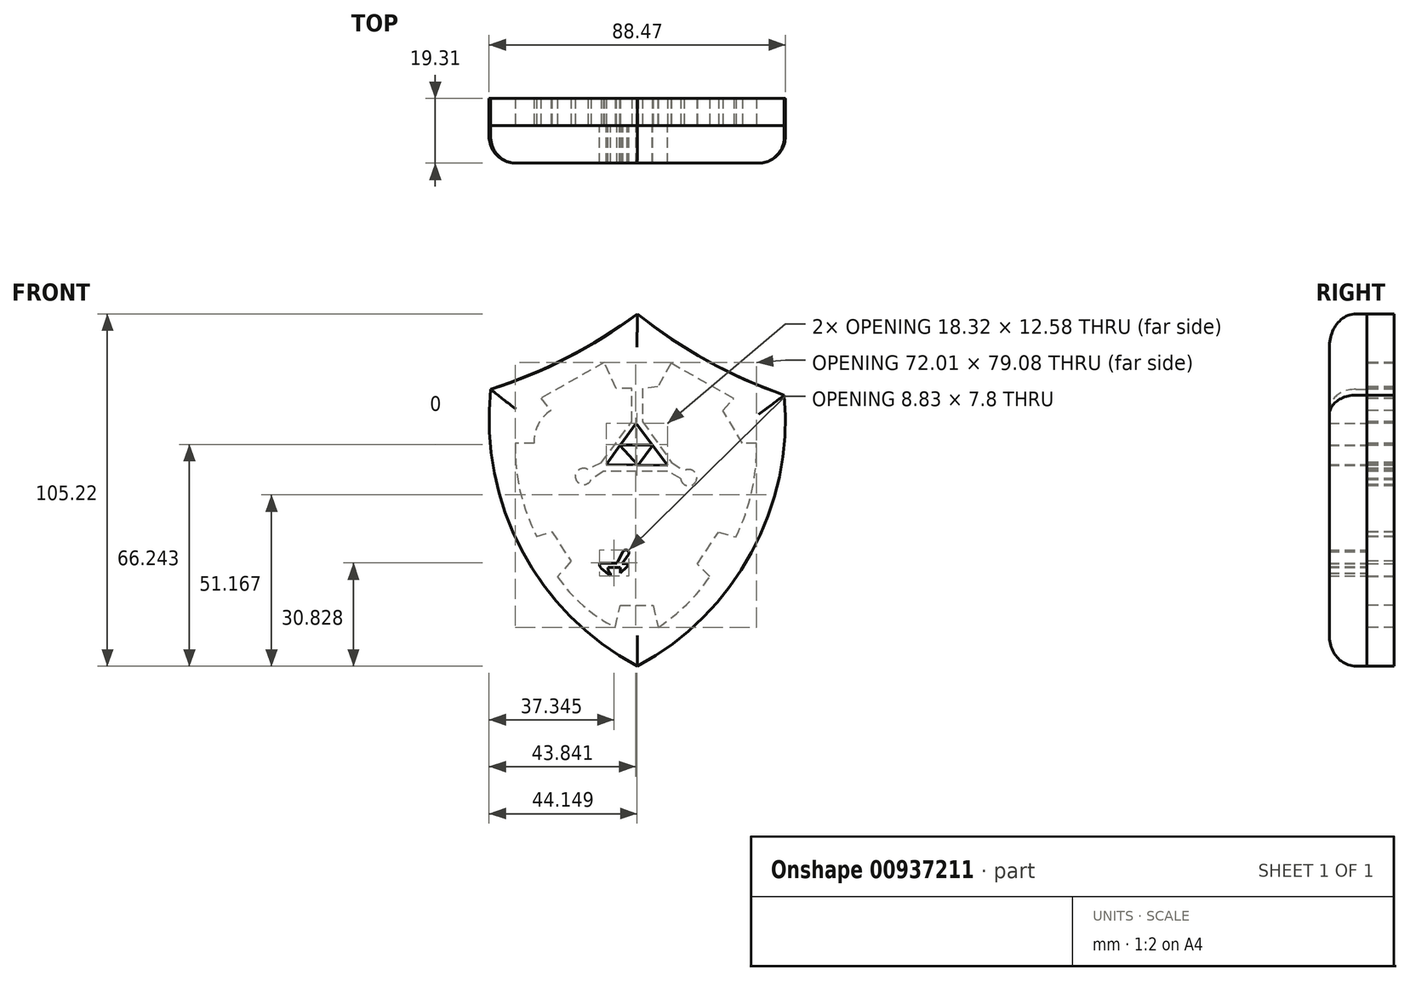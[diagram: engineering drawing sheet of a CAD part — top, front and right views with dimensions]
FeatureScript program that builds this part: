
annotation { "Feature Type Name" : "Feature", "Feature Type Description" : "" }
export const myFeature = defineFeature(function(context is Context, id is Id, definition is map)
    precondition{}
    {
        {
            var Q0;
            Q0=qCreatedBy(makeId("Front.planeOp"),FACE);
            var sketch = newSketch(context, id + "F0", { "sketchPlane" : qUnion([Q0])});
            skArc(sketch, "E0", {"start": v(-56.7, 19.2) * mm, "mid": v(-33.8, 28.57) * mm, "end": v(-12.86, 41.74) * mm});
            skArc(sketch, "E1", {"start": v(-12.86, 41.74) * mm, "mid": v(7.99, 27.67) * mm, "end": v(30.97, 17.46) * mm});
            skArc(sketch, "E2", {"start": v(-12.86, -63.48) * mm, "mid": v(21.2, -29.59) * mm, "end": v(30.97, 17.46) * mm});
            skArc(sketch, "E3", {"start": v(-56.7, 19.2) * mm, "mid": v(-47.44, -28.85) * mm, "end": v(-12.86, -63.48) * mm});
            skLineSegment(sketch, "E4", {"start": v(-8.28, 2.58) * mm, "end": v(-12.7, -3.53) * mm});
            skLineSegment(sketch, "E5", {"start": v(0.36, -13.47) * mm, "end": v(13.66, -8.93) * mm});
            skArc(sketch, "E6", {"start": v(13.66, -8.93) * mm, "mid": v(17.35, -7.44) * mm, "end": v(20.86, -5.56) * mm});
            skArc(sketch, "E7", {"start": v(16.37, -12.5) * mm, "mid": v(19.13, -9.36) * mm, "end": v(20.86, -5.56) * mm});
            skPoint(sketch, "E8", {"position": v(0, -13.58) * mm});
            skLineSegment(sketch, "E9", {"start": v(0, -13.58) * mm, "end": v(0.36, -13.47) * mm});
            skArc(sketch, "E10", {"start": v(0.44, -15.2) * mm, "mid": v(8.46, -14.18) * mm, "end": v(16.37, -12.5) * mm});
            skLineSegment(sketch, "E11", {"start": v(0.44, -15.2) * mm, "end": v(0.44, -17.44) * mm});
            skLineSegment(sketch, "E12", {"start": v(10.97, -17.44) * mm, "end": v(0.44, -17.44) * mm});
            skArc(sketch, "E13", {"start": v(10.97, -17.44) * mm, "mid": v(13.6, -17.2) * mm, "end": v(16.13, -16.53) * mm});
            skLineSegment(sketch, "E14", {"start": v(16.13, -16.53) * mm, "end": v(13.8, -20) * mm});
            skArc(sketch, "E15", {"start": v(0.13, -18.9) * mm, "mid": v(6.9, -20.22) * mm, "end": v(13.8, -20) * mm});
            skArc(sketch, "E16", {"start": v(0.13, -18.9) * mm, "mid": v(-0.5, -19.63) * mm, "end": v(-0.97, -20.5) * mm});
            skLineSegment(sketch, "E17", {"start": v(-0.97, -20.5) * mm, "end": v(6.22, -23.66) * mm});
            skArc(sketch, "E18", {"start": v(6.22, -23.66) * mm, "mid": v(7.7, -24.2) * mm, "end": v(9.22, -24.52) * mm});
            skLineSegment(sketch, "E19", {"start": v(9.22, -24.52) * mm, "end": v(6.35, -25.92) * mm});
            skArc(sketch, "E20", {"start": v(-1.93, -21.78) * mm, "mid": v(1.86, -24.54) * mm, "end": v(6.35, -25.92) * mm});
            skLineSegment(sketch, "E21", {"start": v(-1.93, -21.78) * mm, "end": v(-3.27, -22.73) * mm});
            skLineSegment(sketch, "E22", {"start": v(-3.27, -22.73) * mm, "end": v(-1.17, -26.76) * mm});
            skArc(sketch, "E23", {"start": v(-1.17, -26.76) * mm, "mid": v(-0.43, -27.95) * mm, "end": v(0.5, -29) * mm});
            skLineSegment(sketch, "E24", {"start": v(0.5, -29) * mm, "end": v(-2.2, -29.25) * mm});
            skArc(sketch, "E25", {"start": v(-4.56, -23.5) * mm, "mid": v(-3.82, -26.55) * mm, "end": v(-2.2, -29.25) * mm});
            skArc(sketch, "E26", {"start": v(-8.19, -23.5) * mm, "mid": v(-6.37, -24.18) * mm, "end": v(-4.56, -23.5) * mm});
            skArc(sketch, "E27", {"start": v(-8.44, -20.84) * mm, "mid": v(-8.77, -22.2) * mm, "end": v(-8.19, -23.5) * mm});
            skArc(sketch, "E28", {"start": v(-5.33, -19.98) * mm, "mid": v(-6.92, -20.27) * mm, "end": v(-8.44, -20.84) * mm});
            skArc(sketch, "E29", {"start": v(-5.33, -19.98) * mm, "mid": v(-1.86, -15.18) * mm, "end": v(-3.76, -9.57) * mm});
            skArc(sketch, "E30", {"start": v(0, -13.58) * mm, "mid": v(-1.37, -11.09) * mm, "end": v(-3.76, -9.57) * mm});
            skLineSegment(sketch, "E31", {"start": v(-8.39, -29.34) * mm, "end": v(-6.59, -32.71) * mm});
            skLineSegment(sketch, "E32", {"start": v(-6.59, -32.71) * mm, "end": v(-1.3, -32.71) * mm});
            skLineSegment(sketch, "E33", {"start": v(-8.13, -32.85) * mm, "end": v(-9.98, -30.17) * mm});
            skArc(sketch, "E34", {"start": v(-8.39, -29.34) * mm, "mid": v(-9.65, -28.85) * mm, "end": v(-9.98, -30.17) * mm});
            skLineSegment(sketch, "E35", {"start": v(-8.13, -32.85) * mm, "end": v(-9.24, -32.85) * mm});
            skArc(sketch, "E36", {"start": v(-9.24, -32.85) * mm, "mid": v(-9.74, -33.2) * mm, "end": v(-9.58, -33.79) * mm});
            skLineSegment(sketch, "E37", {"start": v(-9.58, -33.79) * mm, "end": v(-7.63, -35.66) * mm});
            skLineSegment(sketch, "E38", {"start": v(-7.63, -35.66) * mm, "end": v(-7.63, -34.03) * mm});
            skLineSegment(sketch, "E39", {"start": v(-7.63, -34.03) * mm, "end": v(-3.83, -34.03) * mm});
            skArc(sketch, "E40", {"start": v(-4.68, -35.83) * mm, "mid": v(-4.08, -35.02) * mm, "end": v(-3.83, -34.03) * mm});
            skLineSegment(sketch, "E41", {"start": v(-4.68, -35.83) * mm, "end": v(-4.68, -36.55) * mm});
            skLineSegment(sketch, "E42", {"start": v(-4.68, -36.55) * mm, "end": v(-1.91, -34.23) * mm});
            skArc(sketch, "E43", {"start": v(-1.91, -34.23) * mm, "mid": v(-1.42, -33.55) * mm, "end": v(-1.3, -32.71) * mm});
            skLineSegment(sketch, "E44", {"start": v(-12.77, -41.9) * mm, "end": v(-12.13, -38.72) * mm});
            skLineSegment(sketch, "E45", {"start": v(-12.13, -38.72) * mm, "end": v(-11.11, -36.54) * mm});
            skLineSegment(sketch, "E46", {"start": v(-11.11, -36.54) * mm, "end": v(-11.72, -35.83) * mm});
            skLineSegment(sketch, "E47", {"start": v(-11.72, -35.83) * mm, "end": v(-11.72, -32.64) * mm});
            skLineSegment(sketch, "E48", {"start": v(-11.72, -32.64) * mm, "end": v(-11.11, -31.73) * mm});
            skLineSegment(sketch, "E49", {"start": v(-11.11, -31.73) * mm, "end": v(-11.72, -30.74) * mm});
            skArc(sketch, "E50", {"start": v(-10.16, -27.48) * mm, "mid": v(-11.6, -28.8) * mm, "end": v(-11.72, -30.74) * mm});
            skLineSegment(sketch, "E51", {"start": v(-10.16, -27.48) * mm, "end": v(-7.35, -26.45) * mm});
            skLineSegment(sketch, "E52", {"start": v(-7.35, -26.45) * mm, "end": v(-8.57, -26.06) * mm});
            skArc(sketch, "E53", {"start": v(-10.33, -23.17) * mm, "mid": v(-9.98, -24.94) * mm, "end": v(-8.57, -26.06) * mm});
            skLineSegment(sketch, "E54", {"start": v(-10.33, -23.17) * mm, "end": v(-12.43, -21.3) * mm});
            skLineSegment(sketch, "E55", {"start": v(-12.43, -21.3) * mm, "end": v(-12.77, -20.09) * mm});
            skLineSegment(sketch, "E56.MirrorCS", {"start": v(-13.11, -21.3) * mm, "end": v(-12.77, -20.09) * mm});
            skLineSegment(sketch, "E57.MirrorCS", {"start": v(-15.22, -23.17) * mm, "end": v(-13.11, -21.3) * mm});
            skArc(sketch, "E58.MirrorCS", {"start": v(-15.22, -23.17) * mm, "mid": v(-15.57, -24.94) * mm, "end": v(-16.98, -26.06) * mm});
            skLineSegment(sketch, "E59.MirrorCS", {"start": v(-18.2, -26.45) * mm, "end": v(-16.98, -26.06) * mm});
            skLineSegment(sketch, "E60.MirrorCS", {"start": v(-15.39, -27.48) * mm, "end": v(-18.2, -26.45) * mm});
            skArc(sketch, "E61.MirrorCS", {"start": v(-15.39, -27.48) * mm, "mid": v(-13.94, -28.8) * mm, "end": v(-13.83, -30.74) * mm});
            skLineSegment(sketch, "E62.MirrorCS", {"start": v(-14.44, -31.73) * mm, "end": v(-13.83, -30.74) * mm});
            skLineSegment(sketch, "E63.MirrorCS", {"start": v(-13.83, -32.64) * mm, "end": v(-14.44, -31.73) * mm});
            skLineSegment(sketch, "E64.MirrorCS", {"start": v(-13.83, -35.83) * mm, "end": v(-13.83, -32.64) * mm});
            skLineSegment(sketch, "E65.MirrorCS", {"start": v(-14.44, -36.54) * mm, "end": v(-13.83, -35.83) * mm});
            skLineSegment(sketch, "E66.MirrorCS", {"start": v(-13.42, -38.72) * mm, "end": v(-14.44, -36.54) * mm});
            skLineSegment(sketch, "E67.MirrorCS", {"start": v(-12.77, -41.9) * mm, "end": v(-13.42, -38.72) * mm});
            skLineSegment(sketch, "E68", {"start": v(-13.2, -19.23) * mm, "end": v(-12.64, -19.23) * mm});
            skLineSegment(sketch, "E69", {"start": v(-12.64, -19.23) * mm, "end": v(-12.64, -17.45) * mm});
            skArc(sketch, "E70", {"start": v(-11.68, -17.77) * mm, "mid": v(-12.07, -17.33) * mm, "end": v(-12.64, -17.45) * mm});
            skLineSegment(sketch, "E71", {"start": v(-11.68, -17.77) * mm, "end": v(-11.2, -16.54) * mm});
            skLineSegment(sketch, "E72", {"start": v(-11.2, -16.54) * mm, "end": v(-10.34, -17.77) * mm});
            skArc(sketch, "E73", {"start": v(-10.34, -17.77) * mm, "mid": v(-9.81, -17.81) * mm, "end": v(-9.86, -17.29) * mm});
            skArc(sketch, "E74", {"start": v(-10.17, -15.87) * mm, "mid": v(-10.2, -16.62) * mm, "end": v(-9.86, -17.29) * mm});
            skArc(sketch, "E75", {"start": v(-8.7, -17.29) * mm, "mid": v(-9.17, -16.3) * mm, "end": v(-10.17, -15.87) * mm});
            skArc(sketch, "E76", {"start": v(-8.7, -17.29) * mm, "mid": v(-8.49, -17.56) * mm, "end": v(-8.27, -17.29) * mm});
            skArc(sketch, "E77", {"start": v(-8.27, -17.29) * mm, "mid": v(-8.93, -15.3) * mm, "end": v(-10, -13.52) * mm});
            skArc(sketch, "E78", {"start": v(-12.64, -9.75) * mm, "mid": v(-11.92, -12.06) * mm, "end": v(-10, -13.52) * mm});
            skArc(sketch, "E79", {"start": v(-12.64, -9.75) * mm, "mid": v(-12.94, -9.54) * mm, "end": v(-13.24, -9.75) * mm});
            skArc(sketch, "E80.MirrorCS", {"start": v(-13.24, -9.75) * mm, "mid": v(-13.96, -12.06) * mm, "end": v(-15.88, -13.52) * mm});
            skArc(sketch, "E81.MirrorCS", {"start": v(-17.6, -17.29) * mm, "mid": v(-16.96, -15.3) * mm, "end": v(-15.88, -13.52) * mm});
            skArc(sketch, "E82.MirrorCS", {"start": v(-17.18, -17.29) * mm, "mid": v(-17.4, -17.56) * mm, "end": v(-17.6, -17.29) * mm});
            skArc(sketch, "E83.MirrorCS", {"start": v(-17.18, -17.29) * mm, "mid": v(-16.7, -16.3) * mm, "end": v(-15.71, -15.87) * mm});
            skArc(sketch, "E84.MirrorCS", {"start": v(-15.71, -15.87) * mm, "mid": v(-15.67, -16.62) * mm, "end": v(-16.02, -17.29) * mm});
            skArc(sketch, "E85.MirrorCS", {"start": v(-15.54, -17.77) * mm, "mid": v(-16.07, -17.81) * mm, "end": v(-16.02, -17.29) * mm});
            skLineSegment(sketch, "E86.MirrorCS", {"start": v(-14.68, -16.54) * mm, "end": v(-15.54, -17.77) * mm});
            skLineSegment(sketch, "E87.MirrorCS", {"start": v(-14.2, -17.77) * mm, "end": v(-14.68, -16.54) * mm});
            skArc(sketch, "E88.MirrorCS", {"start": v(-14.2, -17.77) * mm, "mid": v(-13.81, -17.33) * mm, "end": v(-13.24, -17.45) * mm});
            skLineSegment(sketch, "E89.MirrorCS", {"start": v(-13.24, -19.23) * mm, "end": v(-13.24, -17.45) * mm});
            skArc(sketch, "E90.MirrorCS", {"start": v(-17.16, -29.34) * mm, "mid": v(-15.9, -28.85) * mm, "end": v(-15.56, -30.17) * mm});
            skLineSegment(sketch, "E91.MirrorCS", {"start": v(-17.16, -29.34) * mm, "end": v(-18.96, -32.71) * mm});
            skLineSegment(sketch, "E92.MirrorCS", {"start": v(-17.42, -32.85) * mm, "end": v(-15.56, -30.17) * mm});
            skLineSegment(sketch, "E93.MirrorCS", {"start": v(-17.42, -32.85) * mm, "end": v(-16.3, -32.85) * mm});
            skArc(sketch, "E94.MirrorCS", {"start": v(-16.3, -32.85) * mm, "mid": v(-15.81, -33.2) * mm, "end": v(-15.97, -33.79) * mm});
            skLineSegment(sketch, "E95.MirrorCS", {"start": v(-15.97, -33.79) * mm, "end": v(-17.92, -35.66) * mm});
            skLineSegment(sketch, "E96.MirrorCS", {"start": v(-17.92, -35.66) * mm, "end": v(-17.92, -34.03) * mm});
            skLineSegment(sketch, "E97.MirrorCS", {"start": v(-17.92, -34.03) * mm, "end": v(-21.72, -34.03) * mm});
            skArc(sketch, "E98.MirrorCS", {"start": v(-20.86, -35.83) * mm, "mid": v(-21.47, -35.02) * mm, "end": v(-21.72, -34.03) * mm});
            skLineSegment(sketch, "E99.MirrorCS", {"start": v(-20.86, -35.83) * mm, "end": v(-20.86, -36.55) * mm});
            skLineSegment(sketch, "E100.MirrorCS", {"start": v(-20.86, -36.55) * mm, "end": v(-23.64, -34.23) * mm});
            skArc(sketch, "E101.MirrorCS", {"start": v(-23.64, -34.23) * mm, "mid": v(-24.13, -33.55) * mm, "end": v(-24.24, -32.71) * mm});
            skLineSegment(sketch, "E102.MirrorCS", {"start": v(-18.96, -32.71) * mm, "end": v(-24.24, -32.71) * mm});
            skArc(sketch, "E103.MirrorCS", {"start": v(-25.75, -14) * mm, "mid": v(-24.47, -11.47) * mm, "end": v(-22.12, -9.87) * mm});
            skLineSegment(sketch, "E104.MirrorCS", {"start": v(-26.12, -13.9) * mm, "end": v(-39.55, -9.8) * mm});
            skArc(sketch, "E105.MirrorCS", {"start": v(-39.55, -9.8) * mm, "mid": v(-43.3, -8.43) * mm, "end": v(-46.86, -6.67) * mm});
            skArc(sketch, "E106.MirrorCS", {"start": v(-42.15, -13.45) * mm, "mid": v(-45.01, -10.4) * mm, "end": v(-46.86, -6.67) * mm});
            skArc(sketch, "E107.MirrorCS", {"start": v(-26.14, -15.64) * mm, "mid": v(-34.19, -14.87) * mm, "end": v(-42.15, -13.45) * mm});
            skLineSegment(sketch, "E108.MirrorCS", {"start": v(-26.14, -15.64) * mm, "end": v(-26.07, -17.87) * mm});
            skLineSegment(sketch, "E109.MirrorCS", {"start": v(-36.6, -18.21) * mm, "end": v(-26.07, -17.87) * mm});
            skArc(sketch, "E110.MirrorCS", {"start": v(-36.6, -18.21) * mm, "mid": v(-39.22, -18.07) * mm, "end": v(-41.78, -17.47) * mm});
            skLineSegment(sketch, "E111.MirrorCS", {"start": v(-41.78, -17.47) * mm, "end": v(-39.34, -20.87) * mm});
            skArc(sketch, "E112.MirrorCS", {"start": v(-25.71, -19.32) * mm, "mid": v(-32.44, -20.86) * mm, "end": v(-39.34, -20.87) * mm});
            skArc(sketch, "E113.MirrorCS", {"start": v(-25.71, -19.32) * mm, "mid": v(-25.05, -20.03) * mm, "end": v(-24.56, -20.88) * mm});
            skArc(sketch, "E114.MirrorCS", {"start": v(-23.56, -22.13) * mm, "mid": v(-27.26, -25) * mm, "end": v(-31.7, -26.54) * mm});
            skLineSegment(sketch, "E115.MirrorCS", {"start": v(-24.56, -20.88) * mm, "end": v(-31.65, -24.28) * mm});
            skLineSegment(sketch, "E116.MirrorCS", {"start": v(-34.62, -25.24) * mm, "end": v(-31.7, -26.54) * mm});
            skArc(sketch, "E117.MirrorCS", {"start": v(-31.65, -24.28) * mm, "mid": v(-33.1, -24.86) * mm, "end": v(-34.62, -25.24) * mm});
            skLineSegment(sketch, "E118.MirrorCS", {"start": v(-22.19, -23.03) * mm, "end": v(-24.16, -27.14) * mm});
            skLineSegment(sketch, "E119.MirrorCS", {"start": v(-23.56, -22.13) * mm, "end": v(-22.19, -23.03) * mm});
            skArc(sketch, "E120.MirrorCS", {"start": v(-24.16, -27.14) * mm, "mid": v(-24.86, -28.35) * mm, "end": v(-25.75, -29.43) * mm});
            skLineSegment(sketch, "E121.MirrorCS", {"start": v(-25.75, -29.43) * mm, "end": v(-23.05, -29.6) * mm});
            skArc(sketch, "E122.MirrorCS", {"start": v(-20.87, -23.76) * mm, "mid": v(-21.51, -26.84) * mm, "end": v(-23.05, -29.6) * mm});
            skArc(sketch, "E123.MirrorCS", {"start": v(-17.25, -23.64) * mm, "mid": v(-19.04, -24.39) * mm, "end": v(-20.87, -23.76) * mm});
            skArc(sketch, "E124.MirrorCS", {"start": v(-17.08, -20.98) * mm, "mid": v(-16.7, -22.34) * mm, "end": v(-17.25, -23.64) * mm});
            skArc(sketch, "E125.MirrorCS", {"start": v(-20.22, -20.22) * mm, "mid": v(-18.61, -20.47) * mm, "end": v(-17.08, -20.98) * mm});
            skArc(sketch, "E126.MirrorCS", {"start": v(-20.22, -20.22) * mm, "mid": v(-23.84, -15.54) * mm, "end": v(-22.12, -9.87) * mm});
            skArc(sketch, "E127", {"start": v(12.96, -0.92) * mm, "mid": v(8.7, 10.6) * mm, "end": v(-1.1, 17.98) * mm});
            skArc(sketch, "E128", {"start": v(15.67, -1.42) * mm, "mid": v(10.69, 11.21) * mm, "end": v(-1.1, 17.98) * mm});
            skLineSegment(sketch, "E129", {"start": v(15.67, -1.42) * mm, "end": v(16.88, -3.2) * mm});
            skLineSegment(sketch, "E130", {"start": v(16.88, -3.2) * mm, "end": v(8.75, -5.13) * mm});
            skArc(sketch, "E131", {"start": v(8.75, -5.13) * mm, "mid": v(5.7, -1.88) * mm, "end": v(1.26, -1.7) * mm});
            skLineSegment(sketch, "E132", {"start": v(1.26, -1.7) * mm, "end": v(-6.09, 7.14) * mm});
            skArc(sketch, "E133", {"start": v(-6.09, 7.14) * mm, "mid": v(-5.36, 10.6) * mm, "end": v(-8.3, 12.56) * mm});
            skLineSegment(sketch, "E134", {"start": v(-8.3, 12.56) * mm, "end": v(-9.94, 12.55) * mm});
            skLineSegment(sketch, "E135", {"start": v(-9.94, 12.55) * mm, "end": v(-8.3, 13.91) * mm});
            skArc(sketch, "E136", {"start": v(-3.23, 8.13) * mm, "mid": v(-3.65, 12.88) * mm, "end": v(-8.3, 13.91) * mm});
            skLineSegment(sketch, "E137", {"start": v(-3.23, 8.13) * mm, "end": v(1.69, 2.71) * mm});
            skPoint(sketch, "E137.endSnap0", {"position": v(-2.41, 2.71) * mm});
            skArc(sketch, "E138", {"start": v(9.75, -0.7) * mm, "mid": v(6.62, 3.11) * mm, "end": v(1.69, 2.71) * mm});
            skLineSegment(sketch, "E139", {"start": v(9.75, -0.7) * mm, "end": v(12.96, -0.92) * mm});
            skLineSegment(sketch, "E140.MirrorCS", {"start": v(-16.36, 12.55) * mm, "end": v(-18, 13.91) * mm});
            skLineSegment(sketch, "E141.MirrorCS", {"start": v(-18, 12.56) * mm, "end": v(-16.36, 12.55) * mm});
            skArc(sketch, "E142.MirrorCS", {"start": v(-20.22, 7.14) * mm, "mid": v(-20.94, 10.6) * mm, "end": v(-18, 12.56) * mm});
            skLineSegment(sketch, "E143.MirrorCS", {"start": v(-27.56, -1.7) * mm, "end": v(-20.22, 7.14) * mm});
            skArc(sketch, "E144.MirrorCS", {"start": v(-35.05, -5.13) * mm, "mid": v(-32.01, -1.88) * mm, "end": v(-27.56, -1.7) * mm});
            skLineSegment(sketch, "E145.MirrorCS", {"start": v(-43.18, -3.2) * mm, "end": v(-35.05, -5.13) * mm});
            skLineSegment(sketch, "E146.MirrorCS", {"start": v(-41.97, -1.42) * mm, "end": v(-43.18, -3.2) * mm});
            skArc(sketch, "E147.MirrorCS", {"start": v(-41.97, -1.42) * mm, "mid": v(-36.99, 11.21) * mm, "end": v(-25.2, 17.98) * mm});
            skArc(sketch, "E148.MirrorCS", {"start": v(-39.26, -0.92) * mm, "mid": v(-35, 10.6) * mm, "end": v(-25.2, 17.98) * mm});
            skLineSegment(sketch, "E149.MirrorCS", {"start": v(-36.05, -0.7) * mm, "end": v(-39.26, -0.92) * mm});
            skArc(sketch, "E150.MirrorCS", {"start": v(-36.05, -0.7) * mm, "mid": v(-32.92, 3.11) * mm, "end": v(-27.99, 2.71) * mm});
            skLineSegment(sketch, "E151.MirrorCS", {"start": v(-23.07, 8.13) * mm, "end": v(-27.99, 2.71) * mm});
            skArc(sketch, "E152.MirrorCS", {"start": v(-23.07, 8.13) * mm, "mid": v(-22.65, 12.88) * mm, "end": v(-18, 13.91) * mm});
            skLineSegment(sketch, "E153", {"start": v(-13.24, 9.05) * mm, "end": v(-3.87, -3.53) * mm});
            skLineSegment(sketch, "E154", {"start": v(-13.24, 9.05) * mm, "end": v(-22.2, -3.26) * mm});
            skLineSegment(sketch, "E155", {"start": v(-22.2, -3.26) * mm, "end": v(-3.87, -3.53) * mm});
            skLineSegment(sketch, "E156", {"start": v(-11.37, 19.49) * mm, "end": v(-11.37, 9.56) * mm});
            skLineSegment(sketch, "E157", {"start": v(-11.37, 9.56) * mm, "end": v(-2.72, -2.65) * mm});
            skLineSegment(sketch, "E158", {"start": v(-2.72, -2.65) * mm, "end": v(1.01, -5.2) * mm});
            skArc(sketch, "E159", {"start": v(0, -7.4) * mm, "mid": v(4.64, -8.2) * mm, "end": v(1.01, -5.2) * mm});
            skLineSegment(sketch, "E160", {"start": v(-12.7, -5.26) * mm, "end": v(-3.91, -5.26) * mm});
            skLineSegment(sketch, "E161", {"start": v(0, -7.4) * mm, "end": v(-3.91, -5.26) * mm});
            skLineSegment(sketch, "E162", {"start": v(-23.69, -2.73) * mm, "end": v(-27.68, -4.76) * mm});
            skArc(sketch, "E163", {"start": v(-27.68, -4.76) * mm, "mid": v(-31.3, -7.56) * mm, "end": v(-26.73, -7.81) * mm});
            skLineSegment(sketch, "E164", {"start": v(-23.69, -2.73) * mm, "end": v(-14.52, 9.56) * mm});
            skLineSegment(sketch, "E165", {"start": v(-14.52, 9.56) * mm, "end": v(-14.52, 19.52) * mm});
            skLineSegment(sketch, "E166", {"start": v(-8.55, -41.43) * mm, "end": v(-5.77, -41.43) * mm});
            skLineSegment(sketch, "E167", {"start": v(-5.77, -41.43) * mm, "end": v(-4.41, -45.04) * mm});
            skLineSegment(sketch, "E168", {"start": v(-8.55, -41.43) * mm, "end": v(-8.55, -42.23) * mm});
            skLineSegment(sketch, "E169", {"start": v(-8.55, -42.23) * mm, "end": v(-6.78, -42.23) * mm});
            skLineSegment(sketch, "E170", {"start": v(-6.78, -42.23) * mm, "end": v(-5.1, -47.88) * mm});
            skPoint(sketch, "E170.endSnap0", {"position": v(-5.1, -43.23) * mm});
            skLineSegment(sketch, "E171", {"start": v(-5.1, -47.88) * mm, "end": v(-2.5, -45.77) * mm});
            skArc(sketch, "E172", {"start": v(-2.5, -45.77) * mm, "mid": v(1.76, -41.27) * mm, "end": v(4.72, -35.83) * mm});
            skArc(sketch, "E173", {"start": v(-4.41, -45.04) * mm, "mid": v(0.42, -40.7) * mm, "end": v(4.72, -35.83) * mm});
            skLineSegment(sketch, "E174", {"start": v(-17.4, -42.56) * mm, "end": v(-20.53, -42.56) * mm});
            skLineSegment(sketch, "E175", {"start": v(-20.53, -42.56) * mm, "end": v(-20.53, -47.92) * mm});
            skArc(sketch, "E176", {"start": v(-30.91, -35.37) * mm, "mid": v(-27.02, -42.72) * mm, "end": v(-20.53, -47.92) * mm});
            skArc(sketch, "E177", {"start": v(-30.91, -35.37) * mm, "mid": v(-26.87, -40.23) * mm, "end": v(-22.07, -44.34) * mm});
            skLineSegment(sketch, "E178", {"start": v(-17.4, -42.56) * mm, "end": v(-17.4, -40.8) * mm});
            skLineSegment(sketch, "E179", {"start": v(-17.4, -40.8) * mm, "end": v(-20.8, -40.8) * mm});
            skLineSegment(sketch, "E180", {"start": v(-20.8, -40.8) * mm, "end": v(-22.07, -44.34) * mm});
            skLineSegment(sketch, "E181", {"start": v(-26.12, -13.9) * mm, "end": v(-25.75, -14) * mm});
            skLineSegment(sketch, "E182", {"start": v(-13.24, -19.23) * mm, "end": v(-13.2, -19.23) * mm});
            skLineSegment(sketch, "E183", {"start": v(-12.7, -5.26) * mm, "end": v(-23, -5.26) * mm});
            skLineSegment(sketch, "E184", {"start": v(-23, -5.26) * mm, "end": v(-26.73, -7.81) * mm});
            skLineSegment(sketch, "E185", {"start": v(-14.52, 19.52) * mm, "end": v(-19.3, 19.52) * mm});
            skLineSegment(sketch, "E186", {"start": v(-19.3, 19.52) * mm, "end": v(-22.8, 27.23) * mm});
            skLineSegment(sketch, "E187", {"start": v(-22.8, 27.23) * mm, "end": v(-41.67, 16.51) * mm});
            skLineSegment(sketch, "E188", {"start": v(-41.67, 16.51) * mm, "end": v(-38.73, 12.85) * mm});
            skArc(sketch, "E189", {"start": v(-38.73, 12.85) * mm, "mid": v(-42.53, 8.63) * mm, "end": v(-43.7, 3.08) * mm});
            skLineSegment(sketch, "E190", {"start": v(-43.7, 3.08) * mm, "end": v(-49.35, 3.08) * mm});
            skArc(sketch, "E191", {"start": v(-49.35, 3.08) * mm, "mid": v(-47.88, -11.24) * mm, "end": v(-42.93, -24.75) * mm});
            skLineSegment(sketch, "E192", {"start": v(-42.93, -24.75) * mm, "end": v(-38.46, -23.27) * mm});
            skLineSegment(sketch, "E193", {"start": v(-38.46, -23.27) * mm, "end": v(-32.68, -32.15) * mm});
            skLineSegment(sketch, "E194", {"start": v(-32.68, -32.15) * mm, "end": v(-36.74, -36.78) * mm});
            skArc(sketch, "E195", {"start": v(-36.74, -36.78) * mm, "mid": v(-29.08, -45.38) * mm, "end": v(-19.56, -51.85) * mm});
            skLineSegment(sketch, "E196", {"start": v(-19.56, -51.85) * mm, "end": v(-17.92, -45.29) * mm});
            skLineSegment(sketch, "E197", {"start": v(-17.92, -45.29) * mm, "end": v(-8.22, -45.29) * mm});
            skLineSegment(sketch, "E198", {"start": v(-8.22, -45.29) * mm, "end": v(-6.65, -51.85) * mm});
            skArc(sketch, "E199", {"start": v(-6.65, -51.85) * mm, "mid": v(1.8, -45.06) * mm, "end": v(8.76, -36.73) * mm});
            skLineSegment(sketch, "E200", {"start": v(8.76, -36.73) * mm, "end": v(4.98, -32.95) * mm});
            skLineSegment(sketch, "E201", {"start": v(4.98, -32.95) * mm, "end": v(11.33, -23.46) * mm});
            skLineSegment(sketch, "E202", {"start": v(11.33, -23.46) * mm, "end": v(16.53, -24.9) * mm});
            skArc(sketch, "E203", {"start": v(16.53, -24.9) * mm, "mid": v(21.27, -11.28) * mm, "end": v(22.67, 3.07) * mm});
            skLineSegment(sketch, "E204", {"start": v(22.67, 3.07) * mm, "end": v(18.53, 3.07) * mm});
            skLineSegment(sketch, "E205", {"start": v(18.53, 3.07) * mm, "end": v(12.68, 12.84) * mm});
            skLineSegment(sketch, "E206", {"start": v(12.68, 12.84) * mm, "end": v(15.9, 16.48) * mm});
            skLineSegment(sketch, "E207", {"start": v(15.9, 16.48) * mm, "end": v(-2.87, 26.96) * mm});
            skLineSegment(sketch, "E208", {"start": v(-2.87, 26.96) * mm, "end": v(-6.8, 19.94) * mm});
            skLineSegment(sketch, "E209", {"start": v(-6.8, 19.94) * mm, "end": v(-11.37, 19.49) * mm});
            skLineSegment(sketch, "E210", {"start": v(-8.28, 2.58) * mm, "end": v(-18.18, 2.58) * mm});
            skLineSegment(sketch, "E211", {"start": v(-18.18, 2.58) * mm, "end": v(-12.7, -3.53) * mm});
            skSolve(sketch);
        }
        {
            var Q0;
            Q0 = qSketchRegion(id + "F0", true);
            var Q1;
            Q1=makeQuery(id+"F0.imprint","IMPRINT",FACE,{"disambiguationData":[TD([[makeQuery(id+"F0.imprint","IMPRINT",EDGE,{"derivedFrom":sQuery(id+"F0.wireOp",EDGE,"E5")}),-1.0]])]});
            var Q2;
            {var subQ0=sQuery(id+"F0.wireOp",EDGE,"E104.MirrorCS");Q2=makeQuery(id+"F0.imprint","IMPRINT",FACE,{"disambiguationData":[TD([[makeQuery(id+"F0.imprint","IMPRINT",EDGE,{"derivedFrom":subQ0}),1.0]])]});}
            var Q3;
            Q3=makeQuery(id+"F0.imprint","IMPRINT",FACE,{"disambiguationData":[TD([[makeQuery(id+"F0.imprint","IMPRINT",EDGE,{"derivedFrom":sQuery(id+"F0.wireOp",EDGE,"E44")}),1.0]])]});
            var Q4;
            Q4=makeQuery(id+"F0.imprint","IMPRINT",FACE,{"disambiguationData":[TD([[makeQuery(id+"F0.imprint","IMPRINT",EDGE,{"derivedFrom":sQuery(id+"F0.wireOp",EDGE,"E31")}),-1.0]])]});
            var Q5;
            Q5=makeQuery(id+"F0.imprint","IMPRINT",FACE,{"disambiguationData":[TD([[makeQuery(id+"F0.imprint","IMPRINT",EDGE,{"derivedFrom":sQuery(id+"F0.wireOp",EDGE,"E90.MirrorCS")}),-1.0]])]});
            var Q6;
            Q6=makeQuery(id+"F0.imprint","IMPRINT",FACE,{"disambiguationData":[TD([[makeQuery(id+"F0.imprint","IMPRINT",EDGE,{"derivedFrom":sQuery(id+"F0.wireOp",EDGE,"E166")}),-1.0]])]});
            var Q7;
            Q7=makeQuery(id+"F0.imprint","IMPRINT",FACE,{"disambiguationData":[TD([[makeQuery(id+"F0.imprint","IMPRINT",EDGE,{"derivedFrom":sQuery(id+"F0.wireOp",EDGE,"E174")}),-1.0]])]});
            var Q8;
            Q8=makeQuery(id+"F0.imprint","IMPRINT",FACE,{"disambiguationData":[TD([[makeQuery(id+"F0.imprint","IMPRINT",EDGE,{"derivedFrom":sQuery(id+"F0.wireOp",EDGE,"E68")}),1.0]])]});
            var Q9;
            Q9=makeQuery(id+"F0.imprint","IMPRINT",FACE,{"disambiguationData":[TD([[makeQuery(id+"F0.imprint","IMPRINT",EDGE,{"derivedFrom":sQuery(id+"F0.wireOp",EDGE,"E140.MirrorCS")}),1.0]])]});
            var Q10;
            {var subQ0=sQuery(id+"F0.wireOp",EDGE,"E153");var subQ1=sQuery(id+"F0.wireOp",EDGE,"E4");var subQ2=makeQuery(id+"F0.imprint","INTERSECT",VERTEX,{"derivedFrom":[subQ1,subQ0]});Q10=makeQuery(id+"F0.imprint","IMPRINT",FACE,{"disambiguationData":[TD([[makeQuery(id+"F0.imprint","IMPRINT",EDGE,{"disambiguationData":[TD([[subQ2,-1.0]])],"derivedFrom":subQ1}),-1.0]])]});}
            var Q11;
            Q11=makeQuery(id+"F0.imprint","IMPRINT",FACE,{"disambiguationData":[TD([[makeQuery(id+"F0.imprint","IMPRINT",EDGE,{"derivedFrom":sQuery(id+"F0.wireOp",EDGE,"E127")}),-1.0]])]});
            extrude(context, id + "F1", {"entities" : qUnion([Q0, Q1, Q2, Q3, Q4, Q5, Q6, Q7, Q8, Q9, Q10, Q11]), "depth" : 11.18 * mm, "offsetDistance" : 25.4 * mm});
        }
        {
            var Q0;
            Q0=makeQuery(id+"F1.opExtrude","CAP_FACE",FACE,{"disambiguationData":[OSD([sQuery(id+"F0.wireOp",EDGE,"E0"),sQuery(id+"F0.wireOp",EDGE,"E1"),sQuery(id+"F0.wireOp",EDGE,"E2"),sQuery(id+"F0.wireOp",EDGE,"E3"),sQuery(id+"F0.wireOp",EDGE,"E4"),sQuery(id+"F0.wireOp",EDGE,"jtcVNIn4-J7lP-QaGF-Q5ER-oHSLckI6yKhu"),sQuery(id+"F0.wireOp",EDGE,"ScjCbCCR-YiaC-CpRJ-x9vB-3i5lEsDzDjJE"),sQuery(id+"F0.wireOp",EDGE,"E153"),sQuery(id+"F0.wireOp",EDGE,"E154"),sQuery(id+"F0.wireOp",EDGE,"E155"),sQuery(id+"F0.wireOp",EDGE,"E156"),sQuery(id+"F0.wireOp",EDGE,"E157"),sQuery(id+"F0.wireOp",EDGE,"E158"),sQuery(id+"F0.wireOp",EDGE,"E159"),sQuery(id+"F0.wireOp",EDGE,"E160"),sQuery(id+"F0.wireOp",EDGE,"E161"),sQuery(id+"F0.wireOp",EDGE,"E162"),sQuery(id+"F0.wireOp",EDGE,"E163"),sQuery(id+"F0.wireOp",EDGE,"E164"),sQuery(id+"F0.wireOp",EDGE,"E165"),sQuery(id+"F0.wireOp",EDGE,"E183"),sQuery(id+"F0.wireOp",EDGE,"E184"),sQuery(id+"F0.wireOp",EDGE,"E185"),sQuery(id+"F0.wireOp",EDGE,"E186"),sQuery(id+"F0.wireOp",EDGE,"E187"),sQuery(id+"F0.wireOp",EDGE,"E188"),sQuery(id+"F0.wireOp",EDGE,"E189"),sQuery(id+"F0.wireOp",EDGE,"E190"),sQuery(id+"F0.wireOp",EDGE,"E191"),sQuery(id+"F0.wireOp",EDGE,"E192"),sQuery(id+"F0.wireOp",EDGE,"E193"),sQuery(id+"F0.wireOp",EDGE,"E194"),sQuery(id+"F0.wireOp",EDGE,"E195"),sQuery(id+"F0.wireOp",EDGE,"E196"),sQuery(id+"F0.wireOp",EDGE,"E197"),sQuery(id+"F0.wireOp",EDGE,"E198"),sQuery(id+"F0.wireOp",EDGE,"E199"),sQuery(id+"F0.wireOp",EDGE,"E200"),sQuery(id+"F0.wireOp",EDGE,"E201"),sQuery(id+"F0.wireOp",EDGE,"E202"),sQuery(id+"F0.wireOp",EDGE,"E203"),sQuery(id+"F0.wireOp",EDGE,"E204"),sQuery(id+"F0.wireOp",EDGE,"E205"),sQuery(id+"F0.wireOp",EDGE,"E206"),sQuery(id+"F0.wireOp",EDGE,"E207"),sQuery(id+"F0.wireOp",EDGE,"E208"),sQuery(id+"F0.wireOp",EDGE,"E209")])],"isStart":true});
            var sketch = newSketch(context, id + "F2", { "sketchPlane" : qUnion([Q0])});
            skArc(sketch, "E212", {"start": v(-30.97, 17.46) * mm, "mid": v(-8.03, 27.74) * mm, "end": v(12.86, 41.74) * mm});
            skArc(sketch, "E213", {"start": v(12.86, 41.74) * mm, "mid": v(33.87, 28.7) * mm, "end": v(56.7, 19.2) * mm});
            skArc(sketch, "E214", {"start": v(12.86, -63.48) * mm, "mid": v(47.37, -28.81) * mm, "end": v(56.7, 19.2) * mm});
            skArc(sketch, "E215", {"start": v(-30.97, 17.46) * mm, "mid": v(-21.2, -29.59) * mm, "end": v(12.86, -63.48) * mm});
            skSolve(sketch);
        }
        {
            var Q0;
            Q0 = qSketchRegion(id + "F2", true);
            var Q1;
            Q1 = qSketchRegion(id + "F0", true);
            extrude(context, id + "F3", {"entities" : qUnion([Q0, Q1]), "depth" : 8.13 * mm, "offsetDistance" : 25.4 * mm});
        }
        {
            var Q0;
            Q0=makeQuery(id+"F1.opExtrude","CAP_EDGE",EDGE,{"disambiguationData":[OSD([sQuery(id+"F0.wireOp",EDGE,"E2")])],"isStart":false});
            var Q1;
            Q1=makeQuery(id+"F1.opExtrude","CAP_EDGE",EDGE,{"disambiguationData":[OSD([sQuery(id+"F0.wireOp",EDGE,"E3")])],"isStart":false});
            var Q2;
            Q2=makeQuery(id+"F1.opExtrude","CAP_EDGE",EDGE,{"disambiguationData":[OSD([sQuery(id+"F0.wireOp",EDGE,"E0")])],"isStart":false});
            var Q3;
            Q3=makeQuery(id+"F1.opExtrude","CAP_EDGE",EDGE,{"disambiguationData":[OSD([sQuery(id+"F0.wireOp",EDGE,"E1")])],"isStart":false});
            fillet(context, id + "F4", {"entities" : qUnion([Q0, Q1, Q2, Q3]), "radius" : 7.97 * mm, "tangentPropagation" : true, "allowEdgeOverflow" : false});
        }
    });
